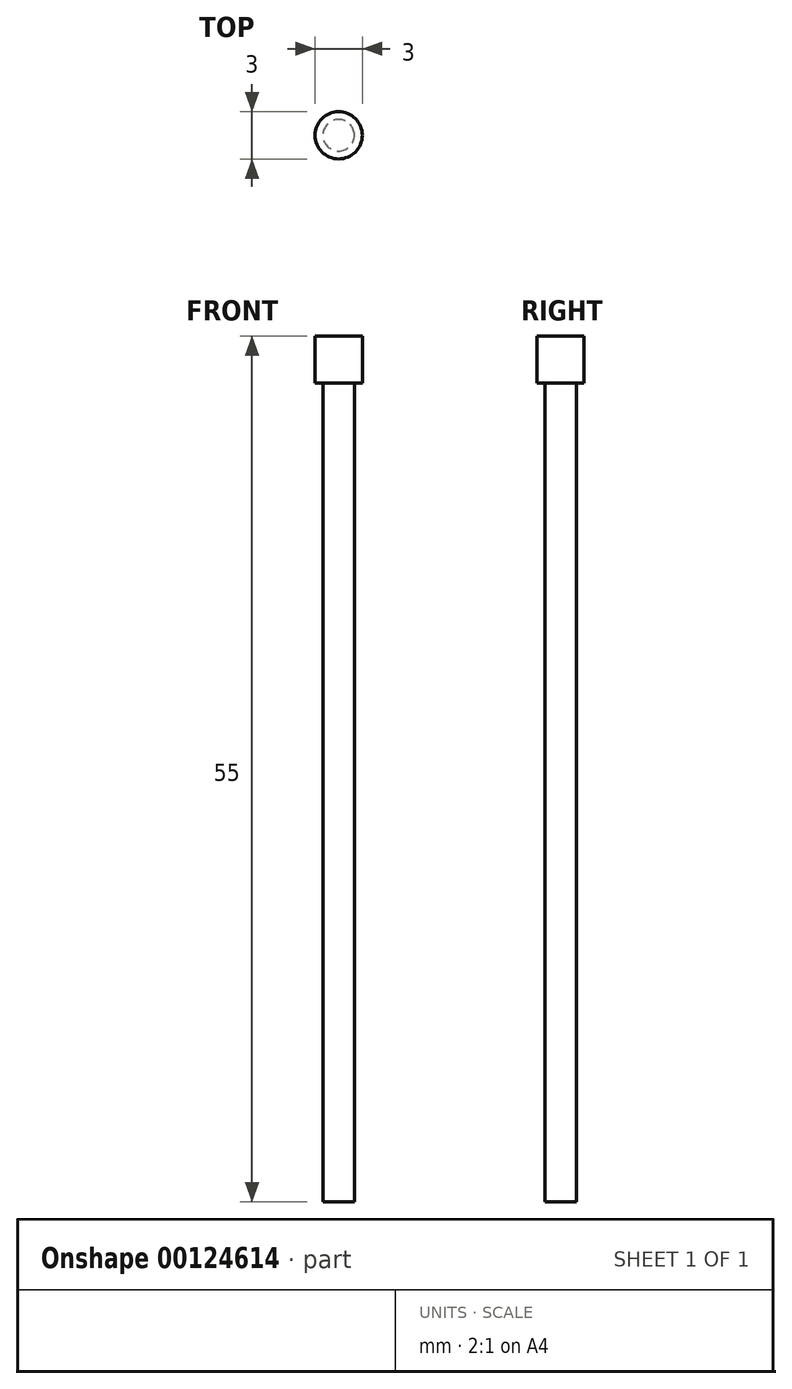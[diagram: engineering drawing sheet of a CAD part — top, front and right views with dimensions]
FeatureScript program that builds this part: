
annotation { "Feature Type Name" : "Feature", "Feature Type Description" : "" }
export const myFeature = defineFeature(function(context is Context, id is Id, definition is map)
    precondition{}
    {
        {
            var Q0;
            Q0=qCreatedBy(makeId("Top.planeOp"),FACE);
            var sketch = newSketch(context, id + "F0", { "sketchPlane" : qUnion([Q0])});
            skCircle(sketch, "E0", {"center": v(0, 0) * mm, "radius": 1 * mm});
            skSolve(sketch);
        }
        {
            var Q0;
            Q0=makeQuery(id+"F0.imprint","IMPRINT",FACE,{"disambiguationData":[TD([[makeQuery(id+"F0.imprint","IMPRINT",EDGE,{"derivedFrom":sQuery(id+"F0.wireOp",EDGE,"E0")}),1.0]])]});
            extrude(context, id + "F1", {"entities" : qUnion([Q0]), "depth" : 52 * mm});
        }
        {
            var Q0;
            Q0=makeQuery(id+"F1.opExtrude","CAP_FACE",FACE,{"disambiguationData":[OSD([sQuery(id+"F0.wireOp",EDGE,"E0")])],"isStart":false});
            var sketch = newSketch(context, id + "F2", { "sketchPlane" : qUnion([Q0])});
            skCircle(sketch, "E1", {"center": v(0, 0) * mm, "radius": 1.5 * mm});
            skSolve(sketch);
        }
        {
            var Q0;
            Q0=makeQuery(id+"F2.imprint","IMPRINT",FACE,{"disambiguationData":[TD([[makeQuery(id+"F2.imprint","IMPRINT",EDGE,{"derivedFrom":sQuery(id+"F2.wireOp",EDGE,"E1")}),1.0]])]});
            var Q1;
            Q1=makeQuery(id+"F2.imprint","IMPRINT",FACE,{"disambiguationData":[TD([[makeQuery(id+"F2.imprint","IMPRINT",EDGE,{"derivedFrom":makeQuery(id+"F1.opExtrude","CAP_EDGE",EDGE,{"disambiguationData":[OSD([sQuery(id+"F0.wireOp",EDGE,"E0")])],"isStart":false})}),1.0]])]});
            extrude(context, id + "F3", {"entities" : qUnion([Q0, Q1]), "operationType" : NewBodyOperationType.ADD, "depth" : 3 * mm});
        }
    });
